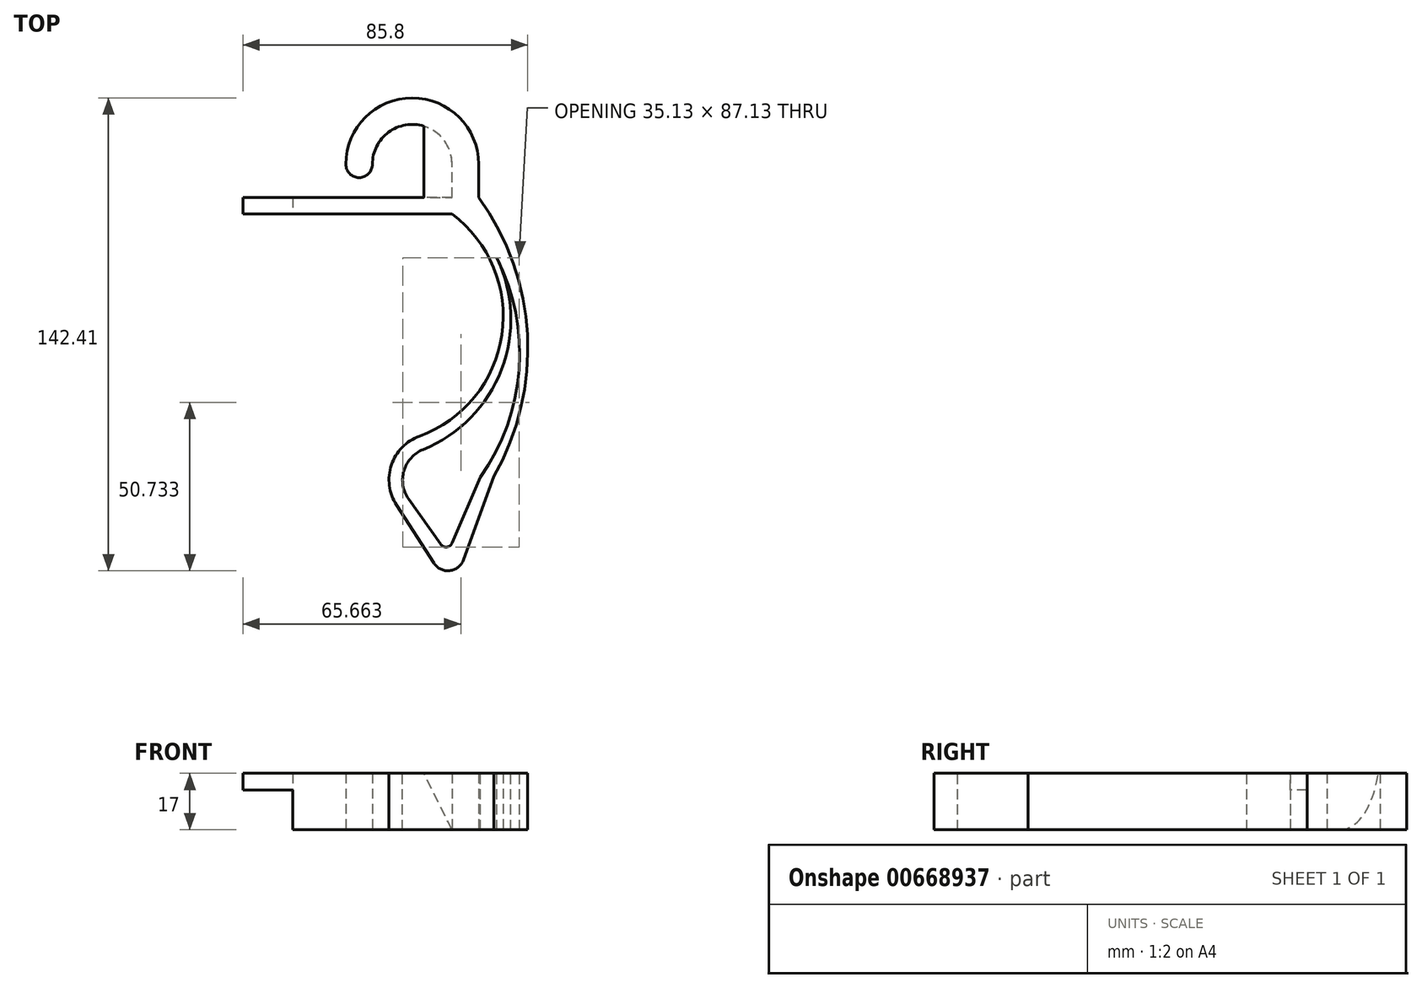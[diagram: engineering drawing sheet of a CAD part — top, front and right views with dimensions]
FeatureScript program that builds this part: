
annotation { "Feature Type Name" : "Feature", "Feature Type Description" : "" }
export const myFeature = defineFeature(function(context is Context, id is Id, definition is map)
    precondition{}
    {
        {
            var Q0;
            Q0=qCreatedBy(makeId("Top.planeOp"),FACE);
            var sketch = newSketch(context, id + "F0", { "sketchPlane" : qUnion([Q0])});
            skLineSegment(sketch, "E0", {"start": v(0, 0) * mm, "end": v(0, -5) * mm});
            skLineSegment(sketch, "E1", {"start": v(0, -5) * mm, "end": v(48, -5) * mm});
            skLineSegment(sketch, "E2", {"start": v(0, 0) * mm, "end": v(48, 0) * mm});
            skLineSegment(sketch, "E3", {"start": v(48, 0) * mm, "end": v(48, 10) * mm});
            skArc(sketch, "E4", {"start": v(48, 10) * mm, "mid": v(36, 22) * mm, "end": v(24, 10) * mm});
            skArc(sketch, "E5", {"start": v(16, 10) * mm, "mid": v(20, 6) * mm, "end": v(24, 10) * mm});
            skArc(sketch, "E6", {"start": v(56, 10) * mm, "mid": v(36, 30) * mm, "end": v(16, 10) * mm});
            skLineSegment(sketch, "E7", {"start": v(36, 31.04) * mm, "end": v(36, 0) * mm, "construction": true});
            skLineSegment(sketch, "E8", {"start": v(9.33, 10) * mm, "end": v(51.81, 10) * mm, "construction": true});
            skLineSegment(sketch, "E9", {"start": v(56, 10) * mm, "end": v(56, 0) * mm});
            skArc(sketch, "E10", {"start": v(38.2, -71.85) * mm, "mid": v(63, -41.35) * mm, "end": v(48, -5) * mm});
            skArc(sketch, "E11", {"start": v(60.56, -83.99) * mm, "mid": v(70.69, -41.32) * mm, "end": v(56, 0) * mm});
            skArc(sketch, "E12", {"start": v(38.2, -71.85) * mm, "mid": v(29.73, -80.55) * mm, "end": v(31.23, -92.59) * mm});
            skLineSegment(sketch, "E13", {"start": v(-21.35, -45.52) * mm, "end": v(30.53, -45.52) * mm, "construction": true});
            skPoint(sketch, "E14", {"position": v(36, 15.52) * mm});
            skLineSegment(sketch, "E15", {"start": v(31.23, -92.59) * mm, "end": v(42.54, -110.12) * mm});
            skLineSegment(sketch, "E16", {"start": v(51.44, -109.11) * mm, "end": v(60.56, -83.99) * mm});
            skPoint(sketch, "E17.visualSharp", {"position": v(48, -118.59) * mm});
            skArc(sketch, "E17.filletArc", {"start": v(42.54, -110.12) * mm, "mid": v(47.3, -112.37) * mm, "end": v(51.44, -109.11) * mm});
            skSolve(sketch);
        }
        {
            var Q0;
            Q0=qSketchRegion(id+"F0",true);
            extrude(context, id + "F1", {"entities" : qUnion([Q0]), "depth" : 17 * mm, "offsetDistance" : 25 * mm});
        }
        {
            var Q0;
            Q0=qCreatedBy(makeId("Top.planeOp"),FACE);
            var sketch = newSketch(context, id + "F2", { "sketchPlane" : qUnion([Q0])});
            skArc(sketch, "E18", {"start": v(39.26, -75.9) * mm, "mid": v(33.48, -82.3) * mm, "end": v(34.9, -90.79) * mm});
            skArc(sketch, "E19", {"start": v(39.26, -75.9) * mm, "mid": v(62.9, -51.82) * mm, "end": v(61.45, -18.11) * mm});
            skArc(sketch, "E20", {"start": v(56.54, -84.2) * mm, "mid": v(68.17, -51.84) * mm, "end": v(61.45, -18.11) * mm});
            skLineSegment(sketch, "E21", {"start": v(34.9, -90.79) * mm, "end": v(44.55, -104.41) * mm});
            skLineSegment(sketch, "E22", {"start": v(48.02, -104.04) * mm, "end": v(56.54, -84.2) * mm});
            skPoint(sketch, "E23.visualSharp", {"position": v(46.61, -107.32) * mm});
            skArc(sketch, "E23.filletArc", {"start": v(44.55, -104.41) * mm, "mid": v(46.4, -105.24) * mm, "end": v(48.02, -104.04) * mm});
            skSolve(sketch);
        }
        {
            var Q0;
            Q0=qSketchRegion(id+"F2",true);
            extrude(context, id + "F3", {"entities" : qUnion([Q0]), "operationType" : NewBodyOperationType.REMOVE, "endBound" : BoundingType.SYMMETRIC, "oppositeDirection" : true, "depth" : 100 * mm, "offsetDistance" : 25 * mm});
        }
        {
            var Q0;
            Q0=makeQuery(id+"F1.opExtrude","SWEPT_FACE",FACE,{"disambiguationData":[OSD([sQuery(id+"F0.wireOp",EDGE,"E2")])]});
            var sketch = newSketch(context, id + "F4", { "sketchPlane" : qUnion([Q0])});
            skLineSegment(sketch, "E24", {"start": v(-48, 17) * mm, "end": v(-48, 0) * mm});
            skLineSegment(sketch, "E25", {"start": v(-48, 0) * mm, "end": v(-39.5, 17) * mm});
            skLineSegment(sketch, "E26", {"start": v(-39.5, 17) * mm, "end": v(-48, 17) * mm});
            skSolve(sketch);
        }
        {
            var Q0;
            Q0=qSketchRegion(id+"F4",true);
            extrude(context, id + "F5", {"entities" : qUnion([Q0]), "operationType" : NewBodyOperationType.ADD, "depth" : 25 * mm, "offsetDistance" : 25 * mm});
        }
        {
            var Q0;
            Q0=makeQuery(id+"F1.opExtrude","SWEPT_FACE",FACE,{"disambiguationData":[OSD([sQuery(id+"F0.wireOp",EDGE,"E0")])]});
            var sketch = newSketch(context, id + "F6", { "sketchPlane" : qUnion([Q0])});
            skLineSegment(sketch, "E27.bottom", {"start": v(-0.02, 12) * mm, "end": v(5, 12) * mm});
            skLineSegment(sketch, "E27.top", {"start": v(-0.02, 17) * mm, "end": v(5, 17) * mm});
            skLineSegment(sketch, "E27.left", {"start": v(-0.02, 12) * mm, "end": v(-0.02, 17) * mm});
            skLineSegment(sketch, "E27.right", {"start": v(5, 12) * mm, "end": v(5, 17) * mm});
            skLineSegment(sketch, "E28", {"start": v(5, 17) * mm, "end": v(5, 12) * mm});
            skSolve(sketch);
        }
        {
            var Q0;
            Q0=qSketchRegion(id+"F6",true);
            extrude(context, id + "F7", {"entities" : qUnion([Q0]), "operationType" : NewBodyOperationType.ADD, "depth" : 15 * mm, "offsetDistance" : 25 * mm});
        }
    });
